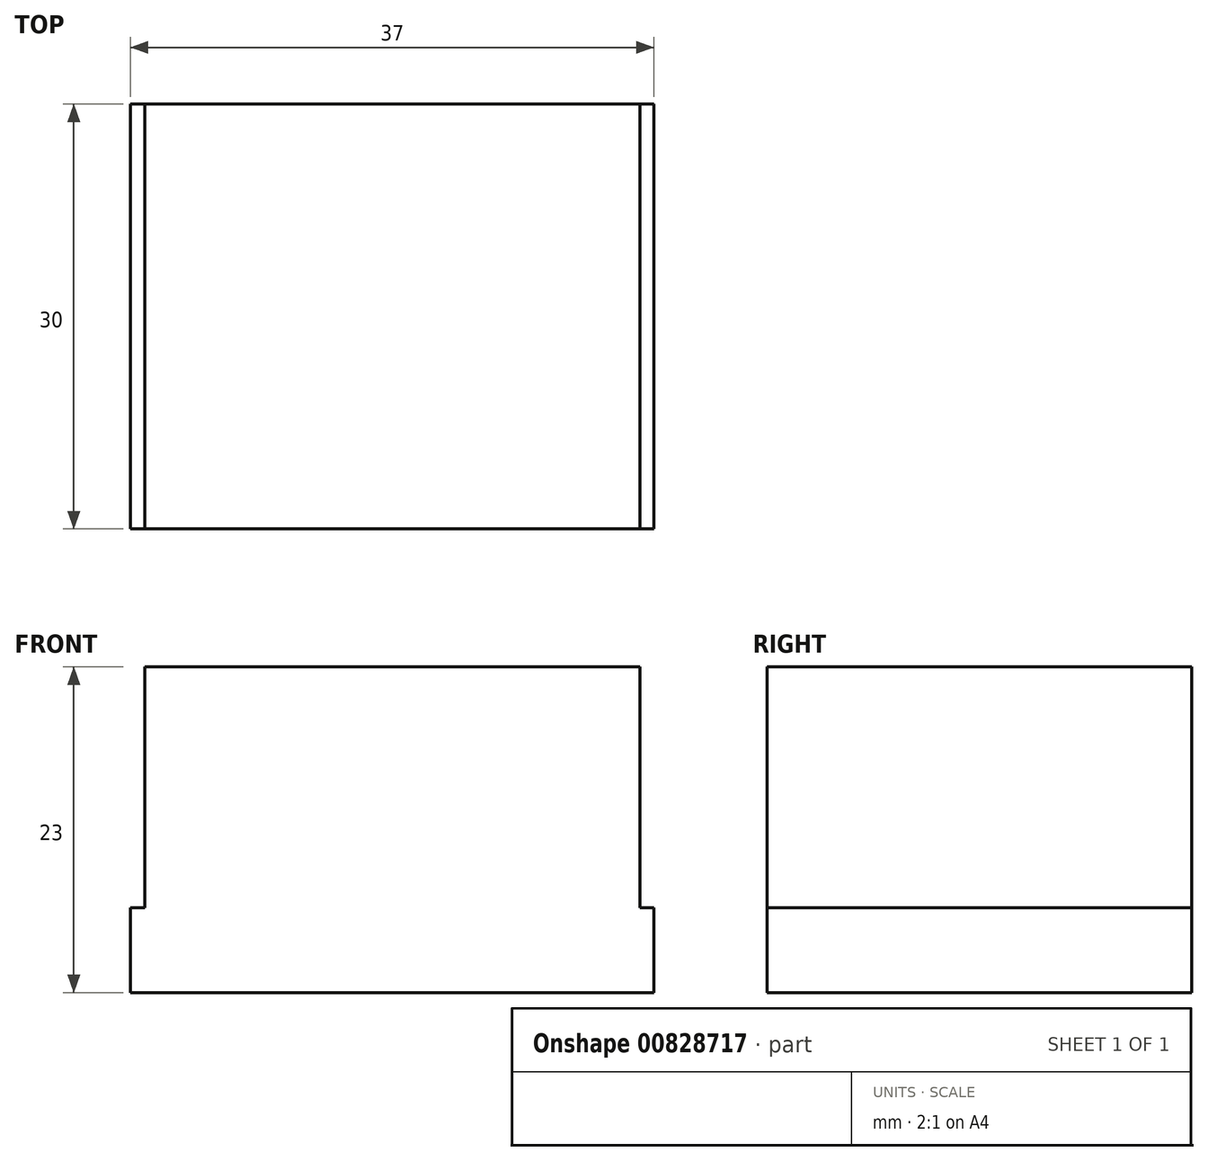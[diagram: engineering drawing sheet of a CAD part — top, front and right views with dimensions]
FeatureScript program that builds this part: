
annotation { "Feature Type Name" : "Feature", "Feature Type Description" : "" }
export const myFeature = defineFeature(function(context is Context, id is Id, definition is map)
    precondition{}
    {
        {
            var Q0;
            Q0=qCreatedBy(makeId("Front.planeOp"),FACE);
            var sketch = newSketch(context, id + "F0", { "sketchPlane" : qUnion([Q0])});
            skLineSegment(sketch, "E0.left", {"start": v(0, 0) * mm, "end": v(0, 0) * mm});
            skLineSegment(sketch, "E1.bottom", {"start": v(0, 0) * mm, "end": v(35, 0) * mm});
            skLineSegment(sketch, "E1.top", {"start": v(0, 17) * mm, "end": v(35, 17) * mm});
            skLineSegment(sketch, "E1.left", {"start": v(0, 0) * mm, "end": v(0, 17) * mm});
            skLineSegment(sketch, "E1.right", {"start": v(35, 0) * mm, "end": v(35, 17) * mm});
            skLineSegment(sketch, "E2", {"start": v(7, 17) * mm, "end": v(7, 0) * mm});
            skLineSegment(sketch, "E3", {"start": v(21, 17) * mm, "end": v(21, 0) * mm});
            skLineSegment(sketch, "E4", {"start": v(28, 17) * mm, "end": v(28, 0) * mm});
            skLineSegment(sketch, "E5", {"start": v(35, 17) * mm, "end": v(35, 0) * mm});
            skLineSegment(sketch, "E6", {"start": v(35, -6) * mm, "end": v(0, -6) * mm});
            skLineSegment(sketch, "E7", {"start": v(0, -6) * mm, "end": v(-1, -6) * mm});
            skLineSegment(sketch, "E8", {"start": v(-1, -6) * mm, "end": v(-1, 0) * mm});
            skLineSegment(sketch, "E9", {"start": v(-1, 0) * mm, "end": v(0, 0) * mm});
            skLineSegment(sketch, "E10", {"start": v(35, 0) * mm, "end": v(36, 0) * mm});
            skLineSegment(sketch, "E11", {"start": v(36, 0) * mm, "end": v(36, -6) * mm});
            skLineSegment(sketch, "E12", {"start": v(36, -6) * mm, "end": v(35, -6) * mm});
            skLineSegment(sketch, "E13", {"start": v(-1, -2) * mm, "end": v(36, -2) * mm});
            skLineSegment(sketch, "E14", {"start": v(14, 17) * mm, "end": v(14, 0) * mm});
            skLineSegment(sketch, "E15", {"start": v(-1, -4) * mm, "end": v(36, -4) * mm});
            skSolve(sketch);
        }
        {
            var Q0;
            {var subQ0=sQuery(id+"F0.wireOp",EDGE,"E1.right");Q0=makeQuery(id+"F0.imprint","IMPRINT",FACE,{"disambiguationData":[TD([[makeQuery(id+"F0.imprint","IMPRINT",EDGE,{"derivedFrom":subQ0}),1.0]])]});}
            var Q1;
            {var subQ0=sQuery(id+"F0.wireOp",EDGE,"gAQGyEay-Irwd-Xnxv-Xek6-tk0VN2AIztuH");Q1=makeQuery(id+"F0.imprint","IMPRINT",FACE,{"disambiguationData":[TD([[makeQuery(id+"F0.imprint","IMPRINT",EDGE,{"derivedFrom":subQ0}),-1.0]])]});}
            var Q2;
            {var subQ0=sQuery(id+"F0.wireOp",EDGE,"E1.left");Q2=makeQuery(id+"F0.imprint","IMPRINT",FACE,{"disambiguationData":[TD([[makeQuery(id+"F0.imprint","IMPRINT",EDGE,{"derivedFrom":subQ0}),-1.0]])]});}
            var Q3;
            {var subQ0=sQuery(id+"F0.wireOp",EDGE,"1puR4SUE-oTSw-wlBC-kZO9-DhgOJnH220vt");Q3=makeQuery(id+"F0.imprint","IMPRINT",FACE,{"disambiguationData":[TD([[makeQuery(id+"F0.imprint","IMPRINT",EDGE,{"derivedFrom":subQ0}),1.0]])]});}
            var Q4;
            {var subQ0=sQuery(id+"F0.wireOp",EDGE,"E3");Q4=makeQuery(id+"F0.imprint","IMPRINT",FACE,{"disambiguationData":[TD([[makeQuery(id+"F0.imprint","IMPRINT",EDGE,{"derivedFrom":subQ0}),-1.0]])]});}
            var Q5;
            {var subQ2=sQuery(id+"F0.wireOp",EDGE,"E4");Q5=makeQuery(id+"F0.imprint","IMPRINT",FACE,{"disambiguationData":[TD([[makeQuery(id+"F0.imprint","IMPRINT",EDGE,{"derivedFrom":subQ2}),1.0]])]});}
            var Q6;
            {var subQ0=sQuery(id+"F0.wireOp",EDGE,"E13");Q6=makeQuery(id+"F0.imprint","IMPRINT",FACE,{"disambiguationData":[TD([[makeQuery(id+"F0.imprint","IMPRINT",EDGE,{"derivedFrom":subQ0}),-1.0]])]});}
            var Q7;
            {var subQ0=sQuery(id+"F0.wireOp",EDGE,"E2");Q7=makeQuery(id+"F0.imprint","IMPRINT",FACE,{"disambiguationData":[TD([[makeQuery(id+"F0.imprint","IMPRINT",EDGE,{"derivedFrom":subQ0}),1.0]])]});}
            var Q8;
            Q8=makeQuery(id+"F0.imprint","IMPRINT",FACE,{"disambiguationData":[TD([[makeQuery(id+"F0.imprint","IMPRINT",EDGE,{"derivedFrom":sQuery(id+"F0.wireOp",EDGE,"E6")}),-1.0]])]});
            var Q9;
            {var subQ8=sQuery(id+"F0.wireOp",EDGE,"E9");Q9=makeQuery(id+"F0.imprint","IMPRINT",FACE,{"disambiguationData":[TD([[makeQuery(id+"F0.imprint","IMPRINT",EDGE,{"derivedFrom":subQ8}),-1.0]])]});}
            var Q10;
            {var subQ0=sQuery(id+"F0.wireOp",EDGE,"E3");Q10=makeQuery(id+"F0.imprint","IMPRINT",FACE,{"disambiguationData":[TD([[makeQuery(id+"F0.imprint","IMPRINT",EDGE,{"derivedFrom":subQ0}),1.0]])]});}
            extrude(context, id + "F1", {"entities" : qUnion([Q0, Q1, Q2, Q3, Q4, Q5, Q6, Q7, Q8, Q9, Q10]), "depth" : 30 * mm, "offsetDistance" : 25 * mm});
        }
    });
